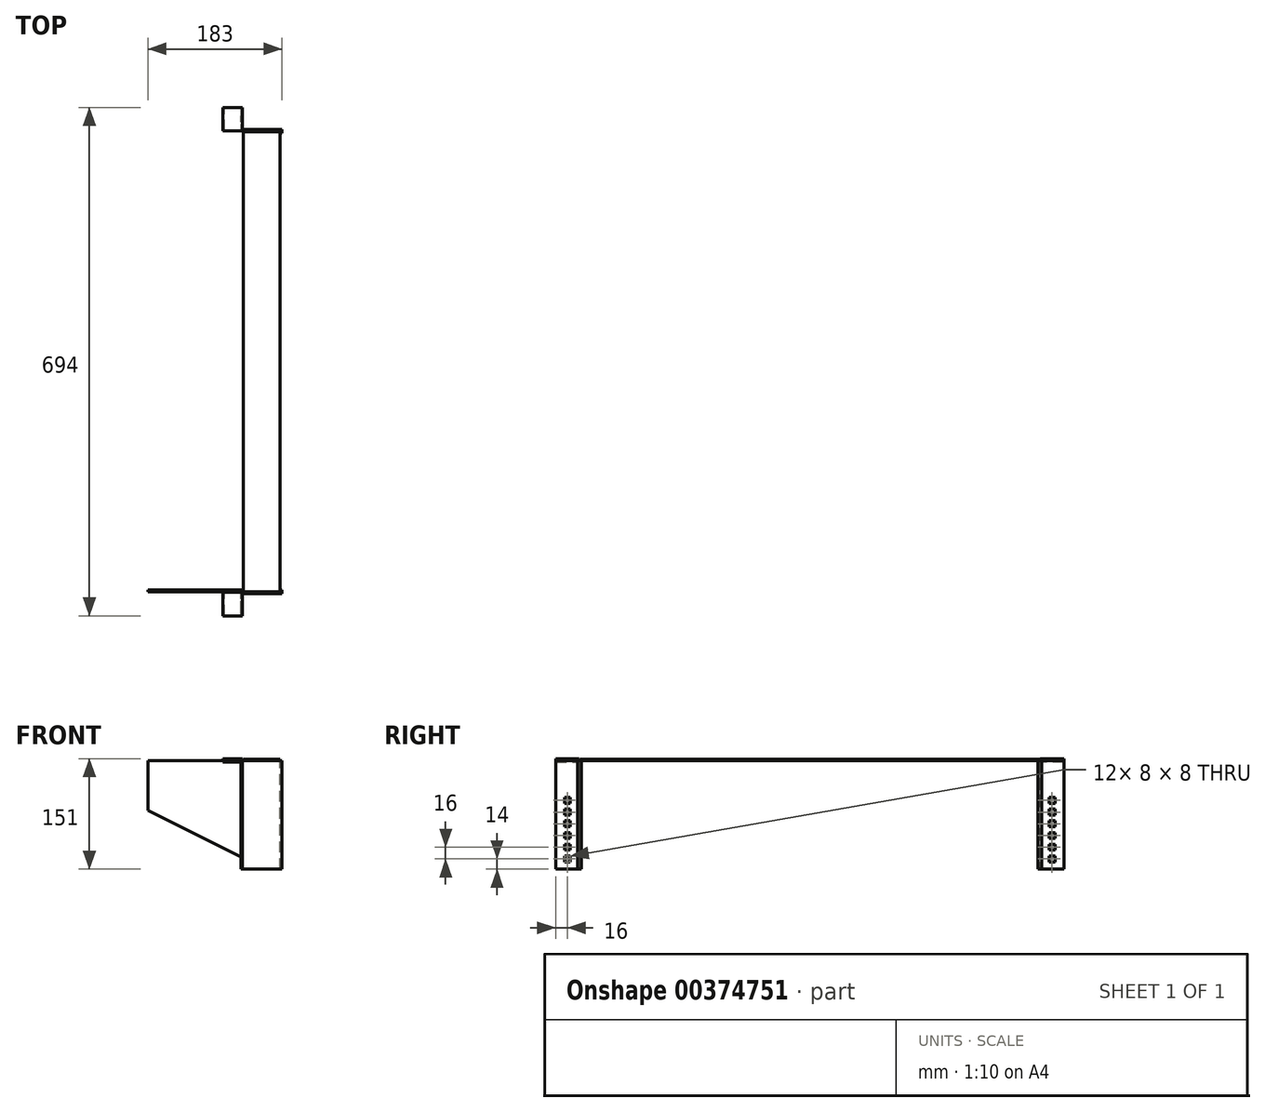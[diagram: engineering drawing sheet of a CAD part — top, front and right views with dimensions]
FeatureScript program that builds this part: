
annotation { "Feature Type Name" : "Feature", "Feature Type Description" : "" }
export const myFeature = defineFeature(function(context is Context, id is Id, definition is map)
    precondition{}
    {
        {
            var Q0;
            Q0=qCreatedBy(makeId("Right.planeOp"),FACE);
            var sketch = newSketch(context, id + "F0", { "sketchPlane" : qUnion([Q0])});
            skLineSegment(sketch, "E0.bottom", {"start": v(-314, 150) * mm, "end": v(314, 150) * mm});
            skLineSegment(sketch, "E0.top", {"start": v(-314, 148) * mm, "end": v(314, 148) * mm});
            skLineSegment(sketch, "E0.left", {"start": v(-314, 150) * mm, "end": v(-314, 148) * mm});
            skLineSegment(sketch, "E0.right", {"start": v(314, 150) * mm, "end": v(314, 148) * mm});
            skLineSegment(sketch, "E1.bottom", {"start": v(-314, 148) * mm, "end": v(-312, 148) * mm});
            skLineSegment(sketch, "E1.top", {"start": v(-314, 0) * mm, "end": v(-312, 0) * mm});
            skLineSegment(sketch, "E1.left", {"start": v(-314, 148) * mm, "end": v(-314, 0) * mm});
            skLineSegment(sketch, "E1.right", {"start": v(-312, 148) * mm, "end": v(-312, 0) * mm});
            skLineSegment(sketch, "E2.bottom", {"start": v(314, 148) * mm, "end": v(312, 148) * mm});
            skLineSegment(sketch, "E2.top", {"start": v(314, 0) * mm, "end": v(312, 0) * mm});
            skLineSegment(sketch, "E2.left", {"start": v(314, 148) * mm, "end": v(314, 0) * mm});
            skLineSegment(sketch, "E2.right", {"start": v(312, 148) * mm, "end": v(312, 0) * mm});
            skSolve(sketch);
        }
        {
            var Q0;
            Q0=makeQuery(id+"F0.imprint","IMPRINT",FACE,{"disambiguationData":[TD([[makeQuery(id+"F0.imprint","IMPRINT",EDGE,{"derivedFrom":sQuery(id+"F0.wireOp",EDGE,"E0.bottom")}),-1.0]])]});
            var Q1;
            Q1=makeQuery(id+"F0.imprint","IMPRINT",FACE,{"disambiguationData":[TD([[makeQuery(id+"F0.imprint","IMPRINT",EDGE,{"derivedFrom":sQuery(id+"F0.wireOp",EDGE,"E2.bottom")}),1.0]])]});
            var Q2;
            Q2=makeQuery(id+"F0.imprint","IMPRINT",FACE,{"disambiguationData":[TD([[makeQuery(id+"F0.imprint","IMPRINT",EDGE,{"derivedFrom":sQuery(id+"F0.wireOp",EDGE,"E1.bottom")}),-1.0]])]});
            extrude(context, id + "F1", {"entities" : qUnion([Q0, Q1, Q2]), "oppositeDirection" : true, "depth" : 50 * mm});
        }
        {
            var Q0;
            Q0=makeQuery(id+"F1.opExtrude","CAP_FACE",FACE,{"disambiguationData":[OSD([sQuery(id+"F0.wireOp",EDGE,"E0.bottom"),sQuery(id+"F0.wireOp",EDGE,"E0.top"),sQuery(id+"F0.wireOp",EDGE,"E0.left"),sQuery(id+"F0.wireOp",EDGE,"E0.right"),sQuery(id+"F0.wireOp",EDGE,"E1.top"),sQuery(id+"F0.wireOp",EDGE,"E1.left"),sQuery(id+"F0.wireOp",EDGE,"E1.right"),sQuery(id+"F0.wireOp",EDGE,"E2.top"),sQuery(id+"F0.wireOp",EDGE,"E2.left"),sQuery(id+"F0.wireOp",EDGE,"E2.right")])],"isStart":false});
            var sketch = newSketch(context, id + "F2", { "sketchPlane" : qUnion([Q0])});
            skLineSegment(sketch, "E3.bottom", {"start": v(314, 0) * mm, "end": v(312, 0) * mm});
            skLineSegment(sketch, "E3.top", {"start": v(314, 150) * mm, "end": v(312, 150) * mm});
            skLineSegment(sketch, "E3.left", {"start": v(314, 0) * mm, "end": v(314, 150) * mm});
            skLineSegment(sketch, "E3.right", {"start": v(312, 0) * mm, "end": v(312, 150) * mm});
            skLineSegment(sketch, "E4.bottom", {"start": v(-312, 0) * mm, "end": v(-314, 0) * mm});
            skLineSegment(sketch, "E4.top", {"start": v(-312, 150) * mm, "end": v(-314, 150) * mm});
            skLineSegment(sketch, "E4.left", {"start": v(-312, 0) * mm, "end": v(-312, 150) * mm});
            skLineSegment(sketch, "E4.right", {"start": v(-314, 0) * mm, "end": v(-314, 150) * mm});
            skSolve(sketch);
        }
        {
            var Q0;
            {var subQ2=sQuery(id+"F2.wireOp",EDGE,"E3.bottom");Q0=makeQuery(id+"F2.imprint","IMPRINT",FACE,{"disambiguationData":[TD([[makeQuery(id+"F2.imprint","IMPRINT",EDGE,{"derivedFrom":subQ2}),-1.0]])]});}
            var Q1;
            {var subQ3=sQuery(id+"F2.wireOp",EDGE,"E4.bottom");Q1=makeQuery(id+"F2.imprint","IMPRINT",FACE,{"disambiguationData":[TD([[makeQuery(id+"F2.imprint","IMPRINT",EDGE,{"derivedFrom":subQ3}),1.0]])]});}
            extrude(context, id + "F3", {"entities" : qUnion([Q0, Q1]), "operationType" : NewBodyOperationType.ADD, "depth" : 130 * mm});
        }
        {
            var Q0;
            Q0=makeQuery(id+"F1.opExtrude","CAP_FACE",FACE,{"disambiguationData":[OSD([sQuery(id+"F0.wireOp",EDGE,"E0.bottom"),sQuery(id+"F0.wireOp",EDGE,"E0.top"),sQuery(id+"F0.wireOp",EDGE,"E0.left"),sQuery(id+"F0.wireOp",EDGE,"E0.right"),sQuery(id+"F0.wireOp",EDGE,"E1.top"),sQuery(id+"F0.wireOp",EDGE,"E1.left"),sQuery(id+"F0.wireOp",EDGE,"E1.right"),sQuery(id+"F0.wireOp",EDGE,"E2.top"),sQuery(id+"F0.wireOp",EDGE,"E2.left"),sQuery(id+"F0.wireOp",EDGE,"E2.right")])],"isStart":true});
            var sketch = newSketch(context, id + "F4", { "sketchPlane" : qUnion([Q0])});
            skLineSegment(sketch, "E5.bottom", {"start": v(314, 0) * mm, "end": v(312, 0) * mm});
            skLineSegment(sketch, "E5.top", {"start": v(314, 148) * mm, "end": v(312, 148) * mm});
            skLineSegment(sketch, "E5.left", {"start": v(314, 0) * mm, "end": v(314, 148) * mm});
            skLineSegment(sketch, "E5.right", {"start": v(312, 0) * mm, "end": v(312, 148) * mm});
            skLineSegment(sketch, "E6.bottom", {"start": v(-312, 0) * mm, "end": v(-314, 0) * mm});
            skLineSegment(sketch, "E6.top", {"start": v(-312, 148) * mm, "end": v(-314, 148) * mm});
            skLineSegment(sketch, "E6.left", {"start": v(-312, 0) * mm, "end": v(-312, 148) * mm});
            skLineSegment(sketch, "E6.right", {"start": v(-314, 0) * mm, "end": v(-314, 148) * mm});
            skSolve(sketch);
        }
        {
            var Q0;
            Q0=makeQuery(id+"F4.imprint","IMPRINT",FACE,{"disambiguationData":[TD([[makeQuery(id+"F4.imprint","IMPRINT",EDGE,{"derivedFrom":sQuery(id+"F4.wireOp",EDGE,"E5.bottom")}),-1.0]])]});
            var Q1;
            Q1=makeQuery(id+"F4.imprint","IMPRINT",FACE,{"disambiguationData":[TD([[makeQuery(id+"F4.imprint","IMPRINT",EDGE,{"derivedFrom":sQuery(id+"F4.wireOp",EDGE,"E6.bottom")}),1.0]])]});
            extrude(context, id + "F5", {"entities" : qUnion([Q0, Q1]), "operationType" : NewBodyOperationType.ADD, "depth" : 3 * mm});
        }
        {
            var Q0;
            Q0=makeQuery(id+"F5.boolean.opBoolean","MERGE",FACE,{"derivedFrom":[makeQuery(id+"F3.boolean.opBoolean","MERGE",FACE,{"derivedFrom":[makeQuery(id+"F1.opExtrude","SWEPT_FACE",FACE,{"disambiguationData":[OSD([sQuery(id+"F0.wireOp",EDGE,"E1.right")])]}),makeQuery(id+"F3.opExtrude","SWEPT_FACE",FACE,{"disambiguationData":[OSD([sQuery(id+"F2.wireOp",EDGE,"E3.right")])]})]}),makeQuery(id+"F5.opExtrude","SWEPT_FACE",FACE,{"disambiguationData":[OSD([sQuery(id+"F4.wireOp",EDGE,"E6.left")])]})]});
            var sketch = newSketch(context, id + "F6", { "sketchPlane" : qUnion([Q0])});
            skLineSegment(sketch, "E7.bottom", {"start": v(-3, 148) * mm, "end": v(-1, 148) * mm});
            skLineSegment(sketch, "E7.top", {"start": v(-3, 0) * mm, "end": v(-1, 0) * mm});
            skLineSegment(sketch, "E7.left", {"start": v(-3, 148) * mm, "end": v(-3, 0) * mm});
            skLineSegment(sketch, "E7.right", {"start": v(-1, 148) * mm, "end": v(-1, 0) * mm});
            skSolve(sketch);
        }
        {
            var Q0;
            Q0=makeQuery(id+"F6.imprint","IMPRINT",FACE,{"disambiguationData":[TD([[makeQuery(id+"F6.imprint","IMPRINT",EDGE,{"derivedFrom":sQuery(id+"F6.wireOp",EDGE,"E7.bottom")}),-1.0]])]});
            extrude(context, id + "F7", {"entities" : qUnion([Q0]), "operationType" : NewBodyOperationType.ADD, "oppositeDirection" : true, "depth" : 5 * mm});
        }
        {
            var Q0;
            Q0=makeQuery(id+"F7.opExtrude","SWEPT_FACE",FACE,{"disambiguationData":[OSD([sQuery(id+"F6.wireOp",EDGE,"E7.right")])]});
            var sketch = newSketch(context, id + "F8", { "sketchPlane" : qUnion([Q0])});
            skLineSegment(sketch, "E8.bottom", {"start": v(315, 0) * mm, "end": v(317, 0) * mm});
            skLineSegment(sketch, "E8.top", {"start": v(315, 148) * mm, "end": v(317, 148) * mm});
            skLineSegment(sketch, "E8.left", {"start": v(317, 0) * mm, "end": v(317, 148) * mm});
            skLineSegment(sketch, "E8.right", {"start": v(315, 0) * mm, "end": v(315, 148) * mm});
            skSolve(sketch);
        }
        {
            var Q0;
            Q0=makeQuery(id+"F8.imprint","IMPRINT",FACE,{"disambiguationData":[TD([[makeQuery(id+"F8.imprint","IMPRINT",EDGE,{"derivedFrom":sQuery(id+"F8.wireOp",EDGE,"E8.bottom")}),-1.0]])]});
            extrude(context, id + "F9", {"entities" : qUnion([Q0]), "operationType" : NewBodyOperationType.ADD, "depth" : 54 * mm});
        }
        {
            var Q0;
            Q0=makeQuery(id+"F9.boolean.opBoolean","MERGE",FACE,{"derivedFrom":[makeQuery(id+"F7.opExtrude","CAP_FACE",FACE,{"disambiguationData":[OSD([sQuery(id+"F6.wireOp",EDGE,"E7.bottom"),sQuery(id+"F6.wireOp",EDGE,"E7.top"),sQuery(id+"F6.wireOp",EDGE,"E7.left"),sQuery(id+"F6.wireOp",EDGE,"E7.right")])],"isStart":false}),makeQuery(id+"F9.opExtrude","SWEPT_FACE",FACE,{"disambiguationData":[OSD([sQuery(id+"F8.wireOp",EDGE,"E8.left")])]})]});
            var sketch = newSketch(context, id + "F10", { "sketchPlane" : qUnion([Q0])});
            skLineSegment(sketch, "E9.bottom", {"start": v(-53, 148) * mm, "end": v(-51, 148) * mm});
            skLineSegment(sketch, "E9.top", {"start": v(-53, 0) * mm, "end": v(-51, 0) * mm});
            skLineSegment(sketch, "E9.left", {"start": v(-53, 148) * mm, "end": v(-53, 0) * mm});
            skLineSegment(sketch, "E9.right", {"start": v(-51, 148) * mm, "end": v(-51, 0) * mm});
            skSolve(sketch);
        }
        {
            var Q0;
            Q0=makeQuery(id+"F10.imprint","IMPRINT",FACE,{"disambiguationData":[TD([[makeQuery(id+"F10.imprint","IMPRINT",EDGE,{"derivedFrom":sQuery(id+"F10.wireOp",EDGE,"E9.bottom")}),1.0]])]});
            extrude(context, id + "F11", {"entities" : qUnion([Q0]), "operationType" : NewBodyOperationType.ADD, "depth" : 30 * mm});
        }
        {
            var Q0;
            Q0=makeQuery(id+"F5.boolean.opBoolean","MERGE",FACE,{"derivedFrom":[makeQuery(id+"F3.boolean.opBoolean","MERGE",FACE,{"derivedFrom":[makeQuery(id+"F1.opExtrude","SWEPT_FACE",FACE,{"disambiguationData":[OSD([sQuery(id+"F0.wireOp",EDGE,"E0.left"),sQuery(id+"F0.wireOp",EDGE,"E1.left")])]}),makeQuery(id+"F3.opExtrude","SWEPT_FACE",FACE,{"disambiguationData":[OSD([sQuery(id+"F2.wireOp",EDGE,"E3.left")])]})]}),makeQuery(id+"F5.opExtrude","SWEPT_FACE",FACE,{"disambiguationData":[OSD([sQuery(id+"F4.wireOp",EDGE,"E6.right")])]})]});
            var sketch = newSketch(context, id + "F12", { "sketchPlane" : qUnion([Q0])});
            skLineSegment(sketch, "E10", {"start": v(0, 0) * mm, "end": v(-20, 0) * mm});
            skLineSegment(sketch, "E11", {"start": v(-20, 0) * mm, "end": v(-180, 80) * mm});
            skLineSegment(sketch, "E12", {"start": v(-180, 80) * mm, "end": v(-180, 0) * mm});
            skLineSegment(sketch, "E13", {"start": v(-180, 0) * mm, "end": v(-20, 0) * mm});
            skSolve(sketch);
        }
        {
            var Q0;
            Q0=makeQuery(id+"F12.imprint","IMPRINT",FACE,{"disambiguationData":[TD([[makeQuery(id+"F12.imprint","IMPRINT",EDGE,{"derivedFrom":sQuery(id+"F12.wireOp",EDGE,"E11")}),1.0]])]});
            extrude(context, id + "F13", {"entities" : qUnion([Q0]), "operationType" : NewBodyOperationType.REMOVE, "oppositeDirection" : true, "depth" : 761 * mm});
        }
        {
            var Q0;
            Q0=makeQuery(id+"F5.boolean.opBoolean","MERGE",FACE,{"derivedFrom":[makeQuery(id+"F3.boolean.opBoolean","MERGE",FACE,{"derivedFrom":[makeQuery(id+"F1.opExtrude","SWEPT_FACE",FACE,{"disambiguationData":[OSD([sQuery(id+"F0.wireOp",EDGE,"E0.right"),sQuery(id+"F0.wireOp",EDGE,"E2.left")])]}),makeQuery(id+"F3.opExtrude","SWEPT_FACE",FACE,{"disambiguationData":[OSD([sQuery(id+"F2.wireOp",EDGE,"E4.right")])]})]}),makeQuery(id+"F5.opExtrude","SWEPT_FACE",FACE,{"disambiguationData":[OSD([sQuery(id+"F4.wireOp",EDGE,"E5.left")])]})]});
            var sketch = newSketch(context, id + "F14", { "sketchPlane" : qUnion([Q0])});
            skLineSegment(sketch, "E14.bottom", {"start": v(-3, 148) * mm, "end": v(-1, 148) * mm});
            skLineSegment(sketch, "E14.top", {"start": v(-3, 0) * mm, "end": v(-1, 0) * mm});
            skLineSegment(sketch, "E14.left", {"start": v(-3, 148) * mm, "end": v(-3, 0) * mm});
            skLineSegment(sketch, "E14.right", {"start": v(-1, 148) * mm, "end": v(-1, 0) * mm});
            skSolve(sketch);
        }
        {
            var Q0;
            Q0=makeQuery(id+"F14.imprint","IMPRINT",FACE,{"disambiguationData":[TD([[makeQuery(id+"F14.imprint","IMPRINT",EDGE,{"derivedFrom":sQuery(id+"F14.wireOp",EDGE,"E14.bottom")}),-1.0]])]});
            extrude(context, id + "F15", {"entities" : qUnion([Q0]), "operationType" : NewBodyOperationType.ADD, "depth" : 3 * mm});
        }
        {
            var Q0;
            Q0=makeQuery(id+"F15.opExtrude","SWEPT_FACE",FACE,{"disambiguationData":[OSD([sQuery(id+"F14.wireOp",EDGE,"E14.right")])]});
            var sketch = newSketch(context, id + "F16", { "sketchPlane" : qUnion([Q0])});
            skLineSegment(sketch, "E15.bottom", {"start": v(-317, 148) * mm, "end": v(-315, 148) * mm});
            skLineSegment(sketch, "E15.top", {"start": v(-317, 0) * mm, "end": v(-315, 0) * mm});
            skLineSegment(sketch, "E15.left", {"start": v(-317, 148) * mm, "end": v(-317, 0) * mm});
            skLineSegment(sketch, "E15.right", {"start": v(-315, 148) * mm, "end": v(-315, 0) * mm});
            skSolve(sketch);
        }
        {
            var Q0;
            Q0 = qSketchRegion(id + "F16", true);
            extrude(context, id + "F17", {"entities" : qUnion([Q0]), "operationType" : NewBodyOperationType.ADD, "depth" : 54 * mm});
        }
        {
            var Q0;
            Q0=makeQuery(id+"F17.boolean.opBoolean","MERGE",FACE,{"derivedFrom":[makeQuery(id+"F15.opExtrude","CAP_FACE",FACE,{"disambiguationData":[OSD([sQuery(id+"F14.wireOp",EDGE,"E14.bottom"),sQuery(id+"F14.wireOp",EDGE,"E14.top"),sQuery(id+"F14.wireOp",EDGE,"E14.left"),sQuery(id+"F14.wireOp",EDGE,"E14.right")])],"isStart":false}),makeQuery(id+"F17.opExtrude","SWEPT_FACE",FACE,{"disambiguationData":[OSD([sQuery(id+"F16.wireOp",EDGE,"E15.left")])]})]});
            var sketch = newSketch(context, id + "F18", { "sketchPlane" : qUnion([Q0])});
            skLineSegment(sketch, "E16.bottom", {"start": v(53, 148) * mm, "end": v(51, 148) * mm});
            skLineSegment(sketch, "E16.top", {"start": v(53, 0) * mm, "end": v(51, 0) * mm});
            skLineSegment(sketch, "E16.left", {"start": v(53, 148) * mm, "end": v(53, 0) * mm});
            skLineSegment(sketch, "E16.right", {"start": v(51, 148) * mm, "end": v(51, 0) * mm});
            skSolve(sketch);
        }
        {
            var Q0;
            Q0=makeQuery(id+"F18.imprint","IMPRINT",FACE,{"disambiguationData":[TD([[makeQuery(id+"F18.imprint","IMPRINT",EDGE,{"derivedFrom":sQuery(id+"F18.wireOp",EDGE,"E16.bottom")}),-1.0]])]});
            extrude(context, id + "F19", {"entities" : qUnion([Q0]), "operationType" : NewBodyOperationType.ADD, "depth" : 30 * mm});
        }
        {
            var Q0;
            Q0=makeQuery(id+"F19.boolean.opBoolean","MERGE",FACE,{"derivedFrom":[makeQuery(id+"F17.opExtrude","CAP_FACE",FACE,{"disambiguationData":[OSD([sQuery(id+"F16.wireOp",EDGE,"E15.bottom"),sQuery(id+"F16.wireOp",EDGE,"E15.top"),sQuery(id+"F16.wireOp",EDGE,"E15.left"),sQuery(id+"F16.wireOp",EDGE,"E15.right")])],"isStart":false}),makeQuery(id+"F19.opExtrude","SWEPT_FACE",FACE,{"disambiguationData":[OSD([sQuery(id+"F18.wireOp",EDGE,"E16.left")])]})]});
            var sketch = newSketch(context, id + "F20", { "sketchPlane" : qUnion([Q0])});
            skLineSegment(sketch, "E17.bottom", {"start": v(-347, 148) * mm, "end": v(-315, 148) * mm});
            skLineSegment(sketch, "E17.top", {"start": v(-347, 146) * mm, "end": v(-315, 146) * mm});
            skLineSegment(sketch, "E17.left", {"start": v(-347, 148) * mm, "end": v(-347, 146) * mm});
            skLineSegment(sketch, "E17.right", {"start": v(-315, 148) * mm, "end": v(-315, 146) * mm});
            skSolve(sketch);
        }
        {
            var Q0;
            Q0=makeQuery(id+"F20.imprint","IMPRINT",FACE,{"disambiguationData":[TD([[makeQuery(id+"F20.imprint","IMPRINT",EDGE,{"derivedFrom":sQuery(id+"F20.wireOp",EDGE,"E17.bottom")}),-1.0]])]});
            extrude(context, id + "F21", {"entities" : qUnion([Q0]), "operationType" : NewBodyOperationType.ADD, "depth" : 25 * mm});
        }
        {
            var Q0;
            Q0=makeQuery(id+"F21.boolean.opBoolean","MERGE",FACE,{"derivedFrom":[makeQuery(id+"F19.boolean.opBoolean","MERGE",FACE,{"derivedFrom":[makeQuery(id+"F17.boolean.opBoolean","MERGE",FACE,{"derivedFrom":[makeQuery(id+"F15.boolean.opBoolean","MERGE",FACE,{"derivedFrom":[makeQuery(id+"F5.opExtrude","SWEPT_FACE",FACE,{"disambiguationData":[OSD([sQuery(id+"F4.wireOp",EDGE,"E5.top")])]}),makeQuery(id+"F15.opExtrude","SWEPT_FACE",FACE,{"disambiguationData":[OSD([sQuery(id+"F14.wireOp",EDGE,"E14.bottom")])]})]}),makeQuery(id+"F17.opExtrude","SWEPT_FACE",FACE,{"disambiguationData":[OSD([sQuery(id+"F16.wireOp",EDGE,"E15.bottom")])]})]}),makeQuery(id+"F19.opExtrude","SWEPT_FACE",FACE,{"disambiguationData":[OSD([sQuery(id+"F18.wireOp",EDGE,"E16.bottom")])]})]}),makeQuery(id+"F21.opExtrude","SWEPT_FACE",FACE,{"disambiguationData":[OSD([sQuery(id+"F20.wireOp",EDGE,"E17.bottom")])]})]});
            var sketch = newSketch(context, id + "F22", { "sketchPlane" : qUnion([Q0])});
            skLineSegment(sketch, "E18.bottom", {"start": v(-78, 315) * mm, "end": v(-76, 315) * mm});
            skLineSegment(sketch, "E18.top", {"start": v(-78, 347) * mm, "end": v(-76, 347) * mm});
            skLineSegment(sketch, "E18.left", {"start": v(-78, 315) * mm, "end": v(-78, 347) * mm});
            skLineSegment(sketch, "E18.right", {"start": v(-76, 315) * mm, "end": v(-76, 347) * mm});
            skSolve(sketch);
        }
        {
            var Q0;
            Q0=makeQuery(id+"F22.imprint","IMPRINT",FACE,{"disambiguationData":[TD([[makeQuery(id+"F22.imprint","IMPRINT",EDGE,{"derivedFrom":sQuery(id+"F22.wireOp",EDGE,"E18.bottom")}),1.0]])]});
            extrude(context, id + "F23", {"entities" : qUnion([Q0]), "operationType" : NewBodyOperationType.ADD, "depth" : 3 * mm});
        }
        {
            var Q0;
            Q0=makeQuery(id+"F23.opExtrude","SWEPT_FACE",FACE,{"disambiguationData":[OSD([sQuery(id+"F22.wireOp",EDGE,"E18.right")])]});
            var sketch = newSketch(context, id + "F24", { "sketchPlane" : qUnion([Q0])});
            skLineSegment(sketch, "E19.bottom", {"start": v(347, 151) * mm, "end": v(315, 151) * mm});
            skLineSegment(sketch, "E19.top", {"start": v(347, 149) * mm, "end": v(315, 149) * mm});
            skLineSegment(sketch, "E19.left", {"start": v(347, 151) * mm, "end": v(347, 149) * mm});
            skLineSegment(sketch, "E19.right", {"start": v(315, 151) * mm, "end": v(315, 149) * mm});
            skSolve(sketch);
        }
        {
            var Q0;
            Q0=makeQuery(id+"F24.imprint","IMPRINT",FACE,{"disambiguationData":[TD([[makeQuery(id+"F24.imprint","IMPRINT",EDGE,{"derivedFrom":sQuery(id+"F24.wireOp",EDGE,"E19.bottom")}),-1.0]])]});
            extrude(context, id + "F25", {"entities" : qUnion([Q0]), "operationType" : NewBodyOperationType.ADD, "depth" : 25 * mm});
        }
        {
            var Q0;
            Q0=makeQuery(id+"F19.boolean.opBoolean","MERGE",FACE,{"derivedFrom":[makeQuery(id+"F17.opExtrude","CAP_FACE",FACE,{"disambiguationData":[OSD([sQuery(id+"F16.wireOp",EDGE,"E15.bottom"),sQuery(id+"F16.wireOp",EDGE,"E15.top"),sQuery(id+"F16.wireOp",EDGE,"E15.left"),sQuery(id+"F16.wireOp",EDGE,"E15.right")])],"isStart":false}),makeQuery(id+"F19.opExtrude","SWEPT_FACE",FACE,{"disambiguationData":[OSD([sQuery(id+"F18.wireOp",EDGE,"E16.left")])]})]});
            var sketch = newSketch(context, id + "F26", { "sketchPlane" : qUnion([Q0])});
            skLineSegment(sketch, "E20.bottom", {"start": v(-327, 10) * mm, "end": v(-335, 10) * mm});
            skLineSegment(sketch, "E20.top", {"start": v(-327, 18) * mm, "end": v(-335, 18) * mm});
            skLineSegment(sketch, "E20.left", {"start": v(-327, 10) * mm, "end": v(-327, 18) * mm});
            skLineSegment(sketch, "E20.right", {"start": v(-335, 10) * mm, "end": v(-335, 18) * mm});
            skLineSegment(sketch, "E21.bottom", {"start": v(-327, 26) * mm, "end": v(-335, 26) * mm});
            skLineSegment(sketch, "E21.top", {"start": v(-327, 34) * mm, "end": v(-335, 34) * mm});
            skLineSegment(sketch, "E21.left", {"start": v(-327, 26) * mm, "end": v(-327, 34) * mm});
            skLineSegment(sketch, "E21.right", {"start": v(-335, 26) * mm, "end": v(-335, 34) * mm});
            skLineSegment(sketch, "E22.bottom", {"start": v(-327, 42) * mm, "end": v(-335, 42) * mm});
            skLineSegment(sketch, "E22.top", {"start": v(-327, 50) * mm, "end": v(-335, 50) * mm});
            skLineSegment(sketch, "E22.left", {"start": v(-327, 42) * mm, "end": v(-327, 50) * mm});
            skLineSegment(sketch, "E22.right", {"start": v(-335, 42) * mm, "end": v(-335, 50) * mm});
            skLineSegment(sketch, "E23.bottom", {"start": v(-327, 58) * mm, "end": v(-335, 58) * mm});
            skLineSegment(sketch, "E23.top", {"start": v(-327, 66) * mm, "end": v(-335, 66) * mm});
            skLineSegment(sketch, "E23.left", {"start": v(-327, 58) * mm, "end": v(-327, 66) * mm});
            skLineSegment(sketch, "E23.right", {"start": v(-335, 58) * mm, "end": v(-335, 66) * mm});
            skLineSegment(sketch, "E24.bottom", {"start": v(-335, 74) * mm, "end": v(-327, 74) * mm});
            skLineSegment(sketch, "E24.top", {"start": v(-335, 82) * mm, "end": v(-327, 82) * mm});
            skLineSegment(sketch, "E24.left", {"start": v(-335, 74) * mm, "end": v(-335, 82) * mm});
            skLineSegment(sketch, "E24.right", {"start": v(-327, 74) * mm, "end": v(-327, 82) * mm});
            skLineSegment(sketch, "E25.bottom", {"start": v(-327, 90) * mm, "end": v(-335, 90) * mm});
            skLineSegment(sketch, "E25.top", {"start": v(-327, 98) * mm, "end": v(-335, 98) * mm});
            skLineSegment(sketch, "E25.left", {"start": v(-327, 90) * mm, "end": v(-327, 98) * mm});
            skLineSegment(sketch, "E25.right", {"start": v(-335, 90) * mm, "end": v(-335, 98) * mm});
            skSolve(sketch);
        }
        {
            var Q0;
            Q0=makeQuery(id+"F26.imprint","IMPRINT",FACE,{"disambiguationData":[TD([[makeQuery(id+"F26.imprint","IMPRINT",EDGE,{"derivedFrom":sQuery(id+"F26.wireOp",EDGE,"E25.bottom")}),-1.0]])]});
            var Q1;
            Q1=makeQuery(id+"F26.imprint","IMPRINT",FACE,{"disambiguationData":[TD([[makeQuery(id+"F26.imprint","IMPRINT",EDGE,{"derivedFrom":sQuery(id+"F26.wireOp",EDGE,"E24.bottom")}),1.0]])]});
            var Q2;
            Q2=makeQuery(id+"F26.imprint","IMPRINT",FACE,{"disambiguationData":[TD([[makeQuery(id+"F26.imprint","IMPRINT",EDGE,{"derivedFrom":sQuery(id+"F26.wireOp",EDGE,"E23.bottom")}),-1.0]])]});
            var Q3;
            Q3=makeQuery(id+"F26.imprint","IMPRINT",FACE,{"disambiguationData":[TD([[makeQuery(id+"F26.imprint","IMPRINT",EDGE,{"derivedFrom":sQuery(id+"F26.wireOp",EDGE,"E22.bottom")}),-1.0]])]});
            var Q4;
            Q4=makeQuery(id+"F26.imprint","IMPRINT",FACE,{"disambiguationData":[TD([[makeQuery(id+"F26.imprint","IMPRINT",EDGE,{"derivedFrom":sQuery(id+"F26.wireOp",EDGE,"E21.bottom")}),-1.0]])]});
            var Q5;
            Q5=makeQuery(id+"F26.imprint","IMPRINT",FACE,{"disambiguationData":[TD([[makeQuery(id+"F26.imprint","IMPRINT",EDGE,{"derivedFrom":sQuery(id+"F26.wireOp",EDGE,"E20.bottom")}),-1.0]])]});
            extrude(context, id + "F27", {"entities" : qUnion([Q0, Q1, Q2, Q3, Q4, Q5]), "operationType" : NewBodyOperationType.REMOVE, "oppositeDirection" : true, "depth" : 25 * mm});
        }
        {
            var Q0;
            Q0=makeQuery(id+"F11.boolean.opBoolean","MERGE",FACE,{"derivedFrom":[makeQuery(id+"F9.opExtrude","CAP_FACE",FACE,{"disambiguationData":[OSD([sQuery(id+"F8.wireOp",EDGE,"E8.bottom"),sQuery(id+"F8.wireOp",EDGE,"E8.top"),sQuery(id+"F8.wireOp",EDGE,"E8.left"),sQuery(id+"F8.wireOp",EDGE,"E8.right")])],"isStart":false}),makeQuery(id+"F11.opExtrude","SWEPT_FACE",FACE,{"disambiguationData":[OSD([sQuery(id+"F10.wireOp",EDGE,"E9.left")])]})]});
            var sketch = newSketch(context, id + "F28", { "sketchPlane" : qUnion([Q0])});
            skLineSegment(sketch, "E26.bottom", {"start": v(347, 148) * mm, "end": v(315, 148) * mm});
            skLineSegment(sketch, "E26.top", {"start": v(347, 146) * mm, "end": v(315, 146) * mm});
            skLineSegment(sketch, "E26.left", {"start": v(347, 148) * mm, "end": v(347, 146) * mm});
            skLineSegment(sketch, "E26.right", {"start": v(315, 148) * mm, "end": v(315, 146) * mm});
            skSolve(sketch);
        }
        {
            var Q0;
            Q0 = qSketchRegion(id + "F28", true);
            extrude(context, id + "F29", {"entities" : qUnion([Q0]), "operationType" : NewBodyOperationType.ADD, "depth" : 25 * mm});
        }
        {
            var Q0;
            Q0=makeQuery(id+"F29.boolean.opBoolean","MERGE",FACE,{"derivedFrom":[makeQuery(id+"F11.boolean.opBoolean","MERGE",FACE,{"derivedFrom":[makeQuery(id+"F9.boolean.opBoolean","MERGE",FACE,{"derivedFrom":[makeQuery(id+"F7.boolean.opBoolean","MERGE",FACE,{"derivedFrom":[makeQuery(id+"F5.opExtrude","SWEPT_FACE",FACE,{"disambiguationData":[OSD([sQuery(id+"F4.wireOp",EDGE,"E6.top")])]}),makeQuery(id+"F7.opExtrude","SWEPT_FACE",FACE,{"disambiguationData":[OSD([sQuery(id+"F6.wireOp",EDGE,"E7.bottom")])]})]}),makeQuery(id+"F9.opExtrude","SWEPT_FACE",FACE,{"disambiguationData":[OSD([sQuery(id+"F8.wireOp",EDGE,"E8.top")])]})]}),makeQuery(id+"F11.opExtrude","SWEPT_FACE",FACE,{"disambiguationData":[OSD([sQuery(id+"F10.wireOp",EDGE,"E9.bottom")])]})]}),makeQuery(id+"F29.opExtrude","SWEPT_FACE",FACE,{"disambiguationData":[OSD([sQuery(id+"F28.wireOp",EDGE,"E26.bottom")])]})]});
            var sketch = newSketch(context, id + "F30", { "sketchPlane" : qUnion([Q0])});
            skLineSegment(sketch, "E27.bottom", {"start": v(-78, -347) * mm, "end": v(-76, -347) * mm});
            skLineSegment(sketch, "E27.top", {"start": v(-78, -315) * mm, "end": v(-76, -315) * mm});
            skLineSegment(sketch, "E27.left", {"start": v(-78, -347) * mm, "end": v(-78, -315) * mm});
            skLineSegment(sketch, "E27.right", {"start": v(-76, -347) * mm, "end": v(-76, -315) * mm});
            skSolve(sketch);
        }
        {
            var Q0;
            Q0 = qSketchRegion(id + "F30", true);
            extrude(context, id + "F31", {"entities" : qUnion([Q0]), "operationType" : NewBodyOperationType.ADD, "depth" : 3 * mm});
        }
        {
            var Q0;
            Q0=makeQuery(id+"F31.opExtrude","SWEPT_FACE",FACE,{"disambiguationData":[OSD([sQuery(id+"F30.wireOp",EDGE,"E27.right")])]});
            var sketch = newSketch(context, id + "F32", { "sketchPlane" : qUnion([Q0])});
            skLineSegment(sketch, "E28.bottom", {"start": v(-347, 151) * mm, "end": v(-315, 151) * mm});
            skLineSegment(sketch, "E28.top", {"start": v(-347, 149) * mm, "end": v(-315, 149) * mm});
            skLineSegment(sketch, "E28.left", {"start": v(-347, 151) * mm, "end": v(-347, 149) * mm});
            skLineSegment(sketch, "E28.right", {"start": v(-315, 151) * mm, "end": v(-315, 149) * mm});
            skSolve(sketch);
        }
        {
            var Q0;
            Q0 = qSketchRegion(id + "F32", true);
            extrude(context, id + "F33", {"entities" : qUnion([Q0]), "operationType" : NewBodyOperationType.ADD, "depth" : 25 * mm});
        }
        {
            var Q0;
            Q0=makeQuery(id+"F11.boolean.opBoolean","MERGE",FACE,{"derivedFrom":[makeQuery(id+"F9.opExtrude","CAP_FACE",FACE,{"disambiguationData":[OSD([sQuery(id+"F8.wireOp",EDGE,"E8.bottom"),sQuery(id+"F8.wireOp",EDGE,"E8.top"),sQuery(id+"F8.wireOp",EDGE,"E8.left"),sQuery(id+"F8.wireOp",EDGE,"E8.right")])],"isStart":false}),makeQuery(id+"F11.opExtrude","SWEPT_FACE",FACE,{"disambiguationData":[OSD([sQuery(id+"F10.wireOp",EDGE,"E9.left")])]})]});
            var sketch = newSketch(context, id + "F34", { "sketchPlane" : qUnion([Q0])});
            skLineSegment(sketch, "E29.bottom", {"start": v(335, 10) * mm, "end": v(327, 10) * mm});
            skLineSegment(sketch, "E29.top", {"start": v(335, 18) * mm, "end": v(327, 18) * mm});
            skLineSegment(sketch, "E29.left", {"start": v(335, 10) * mm, "end": v(335, 18) * mm});
            skLineSegment(sketch, "E29.right", {"start": v(327, 10) * mm, "end": v(327, 18) * mm});
            skLineSegment(sketch, "E30.1.0.0", {"start": v(335, 26) * mm, "end": v(327, 26) * mm});
            skLineSegment(sketch, "E30.1.0.1", {"start": v(335, 26) * mm, "end": v(335, 34) * mm});
            skLineSegment(sketch, "E30.1.0.2", {"start": v(335, 34) * mm, "end": v(327, 34) * mm});
            skLineSegment(sketch, "E30.1.0.3", {"start": v(327, 26) * mm, "end": v(327, 34) * mm});
            skLineSegment(sketch, "E30.2.0.0", {"start": v(335, 42) * mm, "end": v(327, 42) * mm});
            skLineSegment(sketch, "E30.2.0.1", {"start": v(335, 42) * mm, "end": v(335, 50) * mm});
            skLineSegment(sketch, "E30.2.0.2", {"start": v(335, 50) * mm, "end": v(327, 50) * mm});
            skLineSegment(sketch, "E30.2.0.3", {"start": v(327, 42) * mm, "end": v(327, 50) * mm});
            skLineSegment(sketch, "E30.3.0.0", {"start": v(335, 58) * mm, "end": v(327, 58) * mm});
            skLineSegment(sketch, "E30.3.0.1", {"start": v(335, 58) * mm, "end": v(335, 66) * mm});
            skLineSegment(sketch, "E30.3.0.2", {"start": v(335, 66) * mm, "end": v(327, 66) * mm});
            skLineSegment(sketch, "E30.3.0.3", {"start": v(327, 58) * mm, "end": v(327, 66) * mm});
            skLineSegment(sketch, "E30.4.0.0", {"start": v(335, 74) * mm, "end": v(327, 74) * mm});
            skLineSegment(sketch, "E30.4.0.1", {"start": v(335, 74) * mm, "end": v(335, 82) * mm});
            skLineSegment(sketch, "E30.4.0.2", {"start": v(335, 82) * mm, "end": v(327, 82) * mm});
            skLineSegment(sketch, "E30.4.0.3", {"start": v(327, 74) * mm, "end": v(327, 82) * mm});
            skLineSegment(sketch, "E30.5.0.0", {"start": v(335, 90) * mm, "end": v(327, 90) * mm});
            skLineSegment(sketch, "E30.5.0.1", {"start": v(335, 90) * mm, "end": v(335, 98) * mm});
            skLineSegment(sketch, "E30.5.0.2", {"start": v(335, 98) * mm, "end": v(327, 98) * mm});
            skLineSegment(sketch, "E30.5.0.3", {"start": v(327, 90) * mm, "end": v(327, 98) * mm});
            skLineSegment(sketch, "E30.direction1", {"start": v(327, 10) * mm, "end": v(327, 26) * mm, "construction": true});
            skSolve(sketch);
        }
        {
            var Q0;
            Q0=makeQuery(id+"F34.imprint","IMPRINT",FACE,{"disambiguationData":[TD([[makeQuery(id+"F34.imprint","IMPRINT",EDGE,{"derivedFrom":sQuery(id+"F34.wireOp",EDGE,"E30.4.0.0")}),-1.0]])]});
            var Q1;
            Q1=makeQuery(id+"F34.imprint","IMPRINT",FACE,{"disambiguationData":[TD([[makeQuery(id+"F34.imprint","IMPRINT",EDGE,{"derivedFrom":sQuery(id+"F34.wireOp",EDGE,"E30.3.0.0")}),-1.0]])]});
            var Q2;
            Q2=makeQuery(id+"F34.imprint","IMPRINT",FACE,{"disambiguationData":[TD([[makeQuery(id+"F34.imprint","IMPRINT",EDGE,{"derivedFrom":sQuery(id+"F34.wireOp",EDGE,"E30.2.0.0")}),-1.0]])]});
            var Q3;
            Q3=makeQuery(id+"F34.imprint","IMPRINT",FACE,{"disambiguationData":[TD([[makeQuery(id+"F34.imprint","IMPRINT",EDGE,{"derivedFrom":sQuery(id+"F34.wireOp",EDGE,"E30.1.0.0")}),-1.0]])]});
            var Q4;
            Q4=makeQuery(id+"F34.imprint","IMPRINT",FACE,{"disambiguationData":[TD([[makeQuery(id+"F34.imprint","IMPRINT",EDGE,{"derivedFrom":sQuery(id+"F34.wireOp",EDGE,"E29.bottom")}),-1.0]])]});
            var Q5;
            Q5=makeQuery(id+"F34.imprint","IMPRINT",FACE,{"disambiguationData":[TD([[makeQuery(id+"F34.imprint","IMPRINT",EDGE,{"derivedFrom":sQuery(id+"F34.wireOp",EDGE,"E30.5.0.0")}),-1.0]])]});
            extrude(context, id + "F35", {"entities" : qUnion([Q0, Q1, Q2, Q3, Q4, Q5]), "operationType" : NewBodyOperationType.REMOVE, "oppositeDirection" : true, "depth" : 25 * mm});
        }
        {
            var Q0;
            Q0=makeQuery(id+"F5.boolean.opBoolean","MERGE",FACE,{"derivedFrom":[makeQuery(id+"F3.boolean.opBoolean","MERGE",FACE,{"derivedFrom":[makeQuery(id+"F1.opExtrude","SWEPT_FACE",FACE,{"disambiguationData":[OSD([sQuery(id+"F0.wireOp",EDGE,"E0.left"),sQuery(id+"F0.wireOp",EDGE,"E1.left")])]}),makeQuery(id+"F3.opExtrude","SWEPT_FACE",FACE,{"disambiguationData":[OSD([sQuery(id+"F2.wireOp",EDGE,"E3.left")])]})]}),makeQuery(id+"F5.opExtrude","SWEPT_FACE",FACE,{"disambiguationData":[OSD([sQuery(id+"F4.wireOp",EDGE,"E6.right")])]})]});
            var sketch = newSketch(context, id + "F36", { "sketchPlane" : qUnion([Q0])});
            skPoint(sketch, "E31", {"position": v(-100, 85) * mm});
            skSolve(sketch);
        }
        {
            var Q0;
            Q0=sQuery(id+"F36.wireOp",VERTEX,"E31");
            var Q1;
            Q1=makeQuery(id+"F1.opExtrude","SWEPT_BODY",BODY,{"disambiguationData":[OSD([sQuery(id+"F0.wireOp",EDGE,"E0.bottom"),sQuery(id+"F0.wireOp",EDGE,"E0.top"),sQuery(id+"F0.wireOp",EDGE,"E0.left"),sQuery(id+"F0.wireOp",EDGE,"E0.right"),sQuery(id+"F0.wireOp",EDGE,"E1.top"),sQuery(id+"F0.wireOp",EDGE,"E1.left"),sQuery(id+"F0.wireOp",EDGE,"E1.right"),sQuery(id+"F0.wireOp",EDGE,"E2.top"),sQuery(id+"F0.wireOp",EDGE,"E2.left"),sQuery(id+"F0.wireOp",EDGE,"E2.right")])]});
            hole(context, id + "F37", {"style" : HoleStyle.SIMPLE, "endStyle" : HoleEndStyle.THROUGH, "holeDiameter" : 8 * mm, "isTappedThrough" : true, "tappedDepth" : 12 * mm, "tapClearance" : 3, "locations" : qUnion([Q0]), "scope" : qUnion([Q1])});
        }
    });
